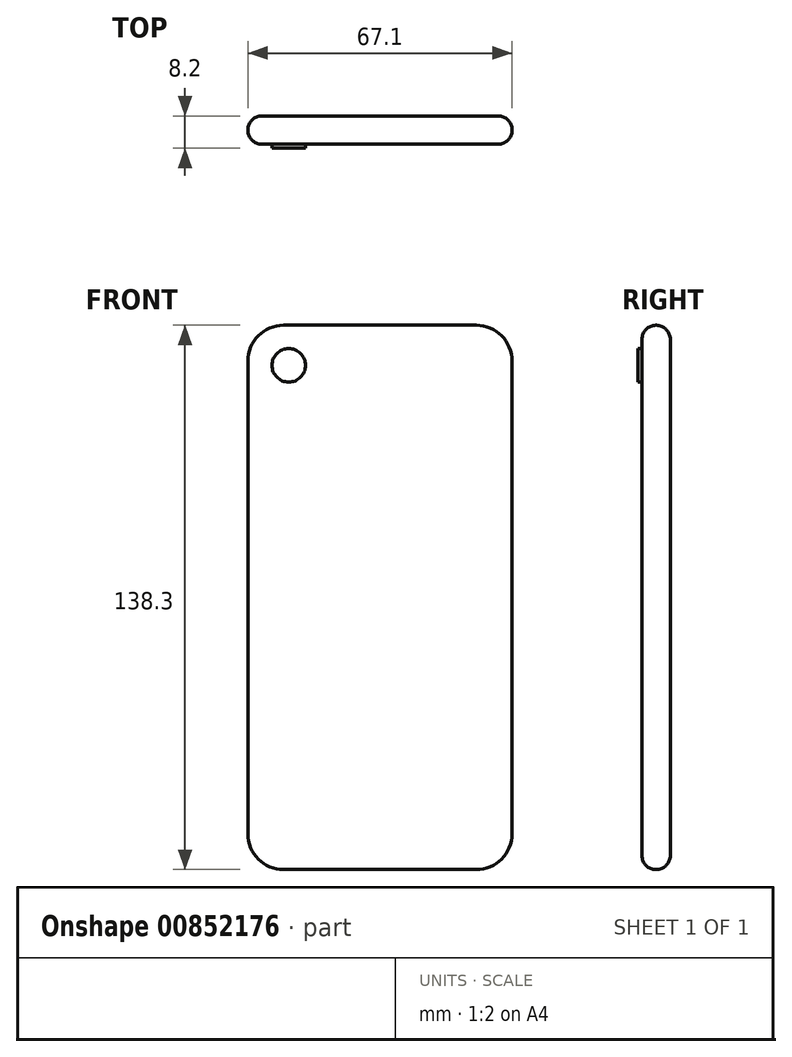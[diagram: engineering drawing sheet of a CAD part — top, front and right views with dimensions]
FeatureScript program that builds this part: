
annotation { "Feature Type Name" : "Feature", "Feature Type Description" : "" }
export const myFeature = defineFeature(function(context is Context, id is Id, definition is map)
    precondition{}
    {
        {
            var Q0;
            Q0=qCreatedBy(makeId("Front.planeOp"),FACE);
            var sketch = newSketch(context, id + "F0", { "sketchPlane" : qUnion([Q0])});
            skLineSegment(sketch, "E0.bottom", {"start": v(-33.55, 0) * mm, "end": v(33.55, 0) * mm});
            skLineSegment(sketch, "E0.top", {"start": v(-33.55, 138.3) * mm, "end": v(33.55, 138.3) * mm});
            skLineSegment(sketch, "E0.left", {"start": v(-33.55, 0) * mm, "end": v(-33.55, 138.3) * mm});
            skLineSegment(sketch, "E0.right", {"start": v(33.55, 0) * mm, "end": v(33.55, 138.3) * mm});
            skSolve(sketch);
        }
        {
            var Q0;
            Q0 = qSketchRegion(id + "F0", true);
            extrude(context, id + "F1", {"entities" : qUnion([Q0]), "depth" : 7.2 * mm, "offsetDistance" : 25 * mm});
        }
        {
            var Q0;
            Q0=makeQuery(id+"F1.opExtrude","CAP_FACE",FACE,{"disambiguationData":[OSD([sQuery(id+"F0.wireOp",EDGE,"E0.bottom"),sQuery(id+"F0.wireOp",EDGE,"E0.top"),sQuery(id+"F0.wireOp",EDGE,"E0.left"),sQuery(id+"F0.wireOp",EDGE,"E0.right")])],"isStart":false});
            var sketch = newSketch(context, id + "F2", { "sketchPlane" : qUnion([Q0])});
            skCircle(sketch, "E1", {"center": v(-23.18, 128.13) * mm, "radius": 4.27 * mm});
            skSolve(sketch);
        }
        {
            var Q0;
            Q0 = qSketchRegion(id + "F2", true);
            extrude(context, id + "F3", {"entities" : qUnion([Q0]), "operationType" : NewBodyOperationType.ADD, "depth" : 1 * mm, "offsetDistance" : 25 * mm});
        }
        {
            var Q0;
            Q0=makeQuery(id+"F1.opExtrude","SWEPT_EDGE",EDGE,{"disambiguationData":[OSD([sQuery(id+"F0.wireOp",EDGE,"E0.top"),sQuery(id+"F0.wireOp",EDGE,"E0.left")])]});
            var Q1;
            Q1=makeQuery(id+"F1.opExtrude","SWEPT_EDGE",EDGE,{"disambiguationData":[OSD([sQuery(id+"F0.wireOp",EDGE,"E0.top"),sQuery(id+"F0.wireOp",EDGE,"E0.right")])]});
            var Q2;
            Q2=makeQuery(id+"F1.opExtrude","SWEPT_EDGE",EDGE,{"disambiguationData":[OSD([sQuery(id+"F0.wireOp",EDGE,"E0.bottom"),sQuery(id+"F0.wireOp",EDGE,"E0.right")])]});
            var Q3;
            Q3=makeQuery(id+"F1.opExtrude","SWEPT_EDGE",EDGE,{"disambiguationData":[OSD([sQuery(id+"F0.wireOp",EDGE,"E0.bottom"),sQuery(id+"F0.wireOp",EDGE,"E0.left")])]});
            fillet(context, id + "F4", {"entities" : qUnion([Q0, Q1, Q2, Q3]), "radius" : 9.08 * mm, "tangentPropagation" : true, "allowEdgeOverflow" : false});
        }
        {
            var Q0;
            Q0=makeQuery(id+"F1.opExtrude","CAP_EDGE",EDGE,{"disambiguationData":[OSD([sQuery(id+"F0.wireOp",EDGE,"E0.top")])],"isStart":false});
            var Q1;
            Q1=makeQuery(id+"F1.opExtrude","CAP_EDGE",EDGE,{"disambiguationData":[OSD([sQuery(id+"F0.wireOp",EDGE,"E0.top")])],"isStart":true});
            fillet(context, id + "F5", {"entities" : qUnion([Q0, Q1]), "radius" : 3.55 * mm, "tangentPropagation" : true, "allowEdgeOverflow" : false});
        }
    });
